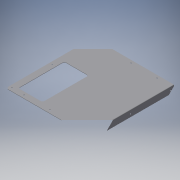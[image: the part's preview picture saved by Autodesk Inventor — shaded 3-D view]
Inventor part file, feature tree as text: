
AUTODESK INVENTOR PART (.ipt)
format: ipt  version: 2016 (Build 200138000, 138)  size: 179,200 bytes
history: native  units: mm
features: other x6, sketch x6, reference x6, sheet_metal_op x4, hole x3, chamfer x1
ambient origin geometry x8: Origin, YZ Plane, XZ Plane, XY Plane, X Axis, Y Axis, Z Axis, Center Point
bodies: Solid1 (feature_tree)
feature tree (26):
  sheet_metal_op  "Face1"
  sheet_metal_op  "Flange1"
  other  "Corner Chamfer1"
  other  "Corner Chamfer2"
  other  "Corner Chamfer3"
  hole  "Hole1"  [1 undecoded]
  hole  "Hole2"  [1 undecoded]
  chamfer  "Corner Round1"
  hole  "Hole3"  [1 undecoded]
  sketch  "Sketch1"  dims[d0=1.0mm d1=1.0mm]
  reference  "Reference1"
  reference  "Reference2"
  reference  "Reference3"
  reference  "Reference4"
  other  "Plate1"
  sketch  "Sketch2"  dims[d2=0.5mm d3=2.0mm]
  other  "Plate2"
  sheet_metal_op  "Bend1"
  sheet_metal_op  "Corner1"
  sketch  "Sketch3"  dims[d4=1.0mm d5=22.0mm d6=90.0deg d7=1.0mm]
  sketch  "Sketch4"  dims[d8=4.0mm]
  sketch  "Sketch5"  dims[d9=1.0mm]
  reference  "Reference5"
  reference  "Reference6"
  sketch  "Sketch6"  dims[d10=1.0mm d11=18.0mm d12=6.0mm d13=45.0deg d14=18.0mm d15=6.0mm d16=45.0deg d17=6.0mm d18=6.0mm d19=45.0deg d20=90.0mm d21=90.0mm d22=10.0mm d23=10.0mm d24=140.0mm d25=140.0mm d26=10.0mm d27=4.0mm d28=6.0mm d29=4.0mm d30=2.0mm d31=90.0deg d32=1.0mm d33=20.594885mm d34=10.0mm d35=140.0mm d36=140.0mm d37=4.0mm d38=6.0mm d39=4.0mm d40=2.0mm d41=90.0deg d42=1.0mm d43=20.594885mm d44=84.0mm d45=160.0mm d46=1.0mm d47=0.0mm d48=6.0mm d49=30.0mm d50=30.0mm d51=8.0mm d52=6.0mm d53=4.0mm d54=2.0mm d55=90.0deg d56=1.0mm d57=20.594885mm]
  other  "Cut1"
note: 3 required parameter values undecoded (feature->parameter linkage not recoverable at this tier; creation-order binding heuristic only, values carry confidence <= 0.55)
